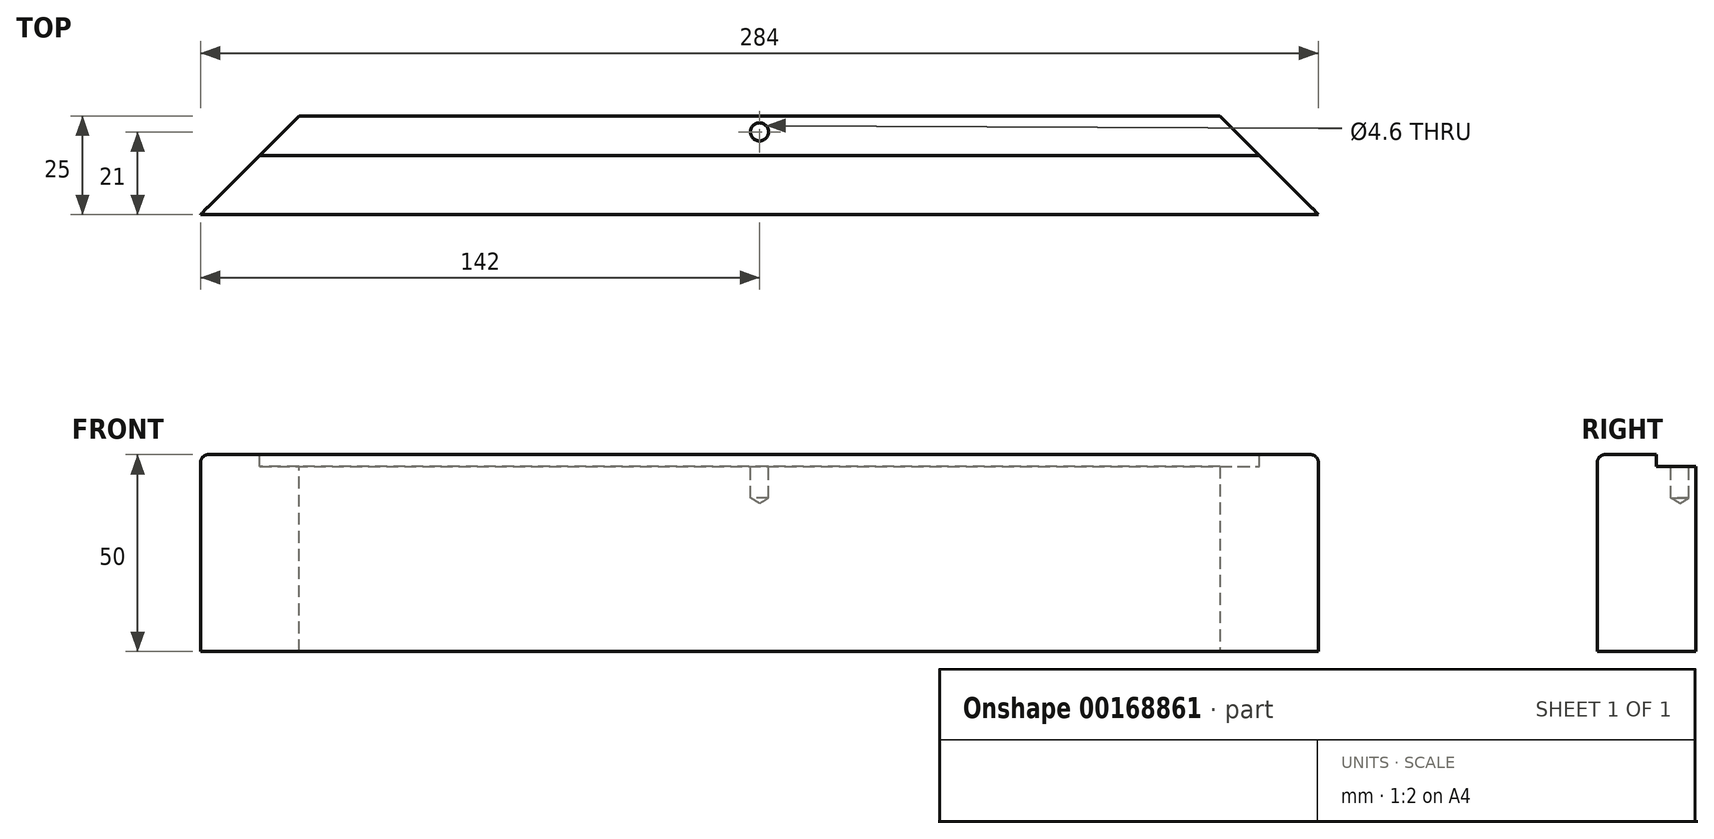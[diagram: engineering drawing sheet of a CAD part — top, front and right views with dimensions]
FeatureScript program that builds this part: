
annotation { "Feature Type Name" : "Feature", "Feature Type Description" : "" }
export const myFeature = defineFeature(function(context is Context, id is Id, definition is map)
    precondition{}
    {
        {
            var Q0;
            Q0=qCreatedBy(makeId("Front.planeOp"),FACE);
            var sketch = newSketch(context, id + "F0", { "sketchPlane" : qUnion([Q0])});
            skLineSegment(sketch, "E0.bottom", {"start": v(142, -25) * mm, "end": v(-142, -25) * mm});
            skLineSegment(sketch, "E0.top", {"start": v(142, 25) * mm, "end": v(-142, 25) * mm});
            skLineSegment(sketch, "E0.left", {"start": v(142, -25) * mm, "end": v(142, 25) * mm});
            skLineSegment(sketch, "E0.right", {"start": v(-142, -25) * mm, "end": v(-142, 25) * mm});
            skLineSegment(sketch, "E1", {"start": v(142, 25) * mm, "end": v(-142, -25) * mm, "construction": true});
            skLineSegment(sketch, "E2", {"start": v(-142, 25) * mm, "end": v(142, -25) * mm, "construction": true});
            skSolve(sketch);
        }
        {
            var Q0;
            Q0=makeQuery(id+"F0.imprint","IMPRINT",FACE,{"disambiguationData":[TD([[makeQuery(id+"F0.imprint","IMPRINT",EDGE,{"derivedFrom":sQuery(id+"F0.wireOp",EDGE,"E0.bottom")}),-1.0]])]});
            var Q1;
            Q1=makeQuery(id+"F0.imprint","IMPRINT",FACE,{"disambiguationData":[TD([[makeQuery(id+"F0.imprint","IMPRINT",EDGE,{"derivedFrom":sQuery(id+"F0.wireOp",EDGE,"TQ8CQex1-5ZuT-i06m-JSEl-Rafa6eQsYN91.left")}),1.0]])]});
            var Q2;
            Q2=makeQuery(id+"F0.imprint","IMPRINT",FACE,{"disambiguationData":[TD([[makeQuery(id+"F0.imprint","IMPRINT",EDGE,{"derivedFrom":sQuery(id+"F0.wireOp",EDGE,"XVRcOiwa-wmZa-OlfB-imAZ-ZysaIvfTFvSH")}),1.0]])]});
            var Q3;
            Q3=makeQuery(id+"F0.imprint","IMPRINT",FACE,{"disambiguationData":[TD([[makeQuery(id+"F0.imprint","IMPRINT",EDGE,{"derivedFrom":sQuery(id+"F0.wireOp",EDGE,"492701c9-3a02-475b-877f-e4fc534a5983")}),1.0]])]});
            var Q4;
            Q4=makeQuery(id+"F0.imprint","IMPRINT",FACE,{"disambiguationData":[TD([[makeQuery(id+"F0.imprint","IMPRINT",EDGE,{"derivedFrom":sQuery(id+"F0.wireOp",EDGE,"TQ8CQex1-5ZuT-i06m-JSEl-Rafa6eQsYN91.right")}),-1.0]])]});
            var Q5;
            {var subQ5=sQuery(id+"F0.wireOp",EDGE,"11b40b25-8dd5-4f7b-a4c1-55c3ff725173.left");Q5=makeQuery(id+"F0.imprint","IMPRINT",FACE,{"disambiguationData":[TD([[makeQuery(id+"F0.imprint","IMPRINT",EDGE,{"derivedFrom":subQ5}),1.0]])]});}
            var Q6;
            {var subQ0=sQuery(id+"F0.wireOp",EDGE,"050ddf37-6dd0-4eab-8f6c-0359ba11038c.filletArc");Q6=makeQuery(id+"F0.imprint","IMPRINT",FACE,{"disambiguationData":[TD([[makeQuery(id+"F0.imprint","IMPRINT",EDGE,{"derivedFrom":subQ0}),1.0]])]});}
            extrude(context, id + "F1", {"entities" : qUnion([Q0, Q1, Q2, Q3, Q4, Q5, Q6]), "depth" : 25 * mm});
        }
        {
            var Q0;
            Q0=makeQuery(id+"F1.opExtrude","CAP_EDGE",EDGE,{"disambiguationData":[OSD([sQuery(id+"F0.wireOp",EDGE,"E0.right")])],"isStart":true});
            var Q1;
            Q1=makeQuery(id+"F1.opExtrude","CAP_EDGE",EDGE,{"disambiguationData":[OSD([sQuery(id+"F0.wireOp",EDGE,"E0.left")])],"isStart":true});
            chamfer(context, id + "F2", {"entities" : qUnion([Q0, Q1]), "width" : 25 * mm, "tangentPropagation" : true});
        }
        {
            var Q0;
            Q0=makeQuery(id+"F1.opExtrude","SWEPT_FACE",FACE,{"disambiguationData":[OSD([sQuery(id+"F0.wireOp",EDGE,"E0.top")])]});
            var sketch = newSketch(context, id + "F3", { "sketchPlane" : qUnion([Q0])});
            skLineSegment(sketch, "E3", {"start": v(-127, -10) * mm, "end": v(127, -10) * mm});
            skLineSegment(sketch, "E4", {"start": v(-134.9, -4) * mm, "end": v(125.52, -4) * mm, "construction": true});
            skLineSegment(sketch, "E5", {"start": v(0, 10.75) * mm, "end": v(0, -16.45) * mm, "construction": true});
            skPoint(sketch, "E5.endSnap0", {"position": v(0, -10) * mm});
            skPoint(sketch, "E6", {"position": v(0, -4) * mm});
            skSolve(sketch);
        }
        {
            var Q0;
            {var subQ0=sQuery(id+"F3.wireOp",EDGE,"E3");Q0=makeQuery(id+"F3.imprint","IMPRINT",FACE,{"disambiguationData":[TD([[makeQuery(id+"F3.imprint","IMPRINT",EDGE,{"derivedFrom":subQ0}),1.0]])]});}
            extrude(context, id + "F4", {"entities" : qUnion([Q0]), "operationType" : NewBodyOperationType.REMOVE, "oppositeDirection" : true, "depth" : 3 * mm});
        }
        {
            var Q0;
            Q0=makeQuery(id+"F4.boolean.opBoolean","COPY",FACE,{"derivedFrom":makeQuery(id+"F4.opExtrude","CAP_FACE",FACE,{"disambiguationData":[OSD([sQuery(id+"F0.wireOp",EDGE,"E0.top"),sQuery(id+"F0.wireOp",EDGE,"E0.left"),sQuery(id+"F0.wireOp",EDGE,"E0.right"),sQuery(id+"F3.wireOp",EDGE,"E3")])],"isStart":false})});
            var sketch = newSketch(context, id + "F5", { "sketchPlane" : qUnion([Q0])});
            skLineSegment(sketch, "E7", {"start": v(-160.86, -4) * mm, "end": v(157.5, -4) * mm, "construction": true});
            skLineSegment(sketch, "E8", {"start": v(0, -19.46) * mm, "end": v(0, 5.76) * mm, "construction": true});
            skPoint(sketch, "E8.startSnap0", {"position": v(0, -10) * mm});
            skPoint(sketch, "E8.endSnap0", {"position": v(0, 0) * mm});
            skPoint(sketch, "E9", {"position": v(0, -4) * mm});
            skSolve(sketch);
        }
        {
            var Q0;
            Q0=sQuery(id+"F5.wireOp",VERTEX,"E9");
            var Q1;
            Q1=makeQuery(id+"F1.opExtrude","SWEPT_BODY",BODY,{"disambiguationData":[OSD([sQuery(id+"F0.wireOp",EDGE,"E0.bottom"),sQuery(id+"F0.wireOp",EDGE,"E0.top"),sQuery(id+"F0.wireOp",EDGE,"E0.left"),sQuery(id+"F0.wireOp",EDGE,"E0.right"),sQuery(id+"F0.wireOp",EDGE,"OmMS4I8q-v5Nw-sNs6-rLWv-C37PQFSncukl.bottom"),sQuery(id+"F0.wireOp",EDGE,"OmMS4I8q-v5Nw-sNs6-rLWv-C37PQFSncukl.top"),sQuery(id+"F0.wireOp",EDGE,"OmMS4I8q-v5Nw-sNs6-rLWv-C37PQFSncukl.left"),sQuery(id+"F0.wireOp",EDGE,"OmMS4I8q-v5Nw-sNs6-rLWv-C37PQFSncukl.right"),sQuery(id+"F0.wireOp",EDGE,"a599c4f8-9d5b-4f08-a6f5-21f0fa9e66a0.filletArc"),sQuery(id+"F0.wireOp",EDGE,"32fc2319-0cb2-45e8-9aa6-fcf55b2109a0.filletArc"),sQuery(id+"F0.wireOp",EDGE,"258bbff2-458d-4a09-ab05-362c01f2241a.filletArc"),sQuery(id+"F0.wireOp",EDGE,"b6ee52c4-7d80-4818-82dd-608125603be5.filletArc")])]});
            hole(context, id + "F6", {"style" : HoleStyle.SIMPLE, "endStyle" : HoleEndStyle.BLIND, "holeDiameter" : 4.6 * mm, "holeDepth" : 8 * mm, "startFromSketch" : true, "locations" : qUnion([Q0]), "scope" : qUnion([Q1])});
        }
        {
            var Q0;
            Q0=makeQuery(id+"F1.opExtrude","CAP_EDGE",EDGE,{"disambiguationData":[OSD([sQuery(id+"F0.wireOp",EDGE,"E0.top")])],"isStart":false});
            fillet(context, id + "F7", {"entities" : qUnion([Q0]), "radius" : 2 * mm, "tangentPropagation" : true, "defaultsChanged" : false, "vertexSettings" : [], "allowEdgeOverflow" : false});
        }
    });
